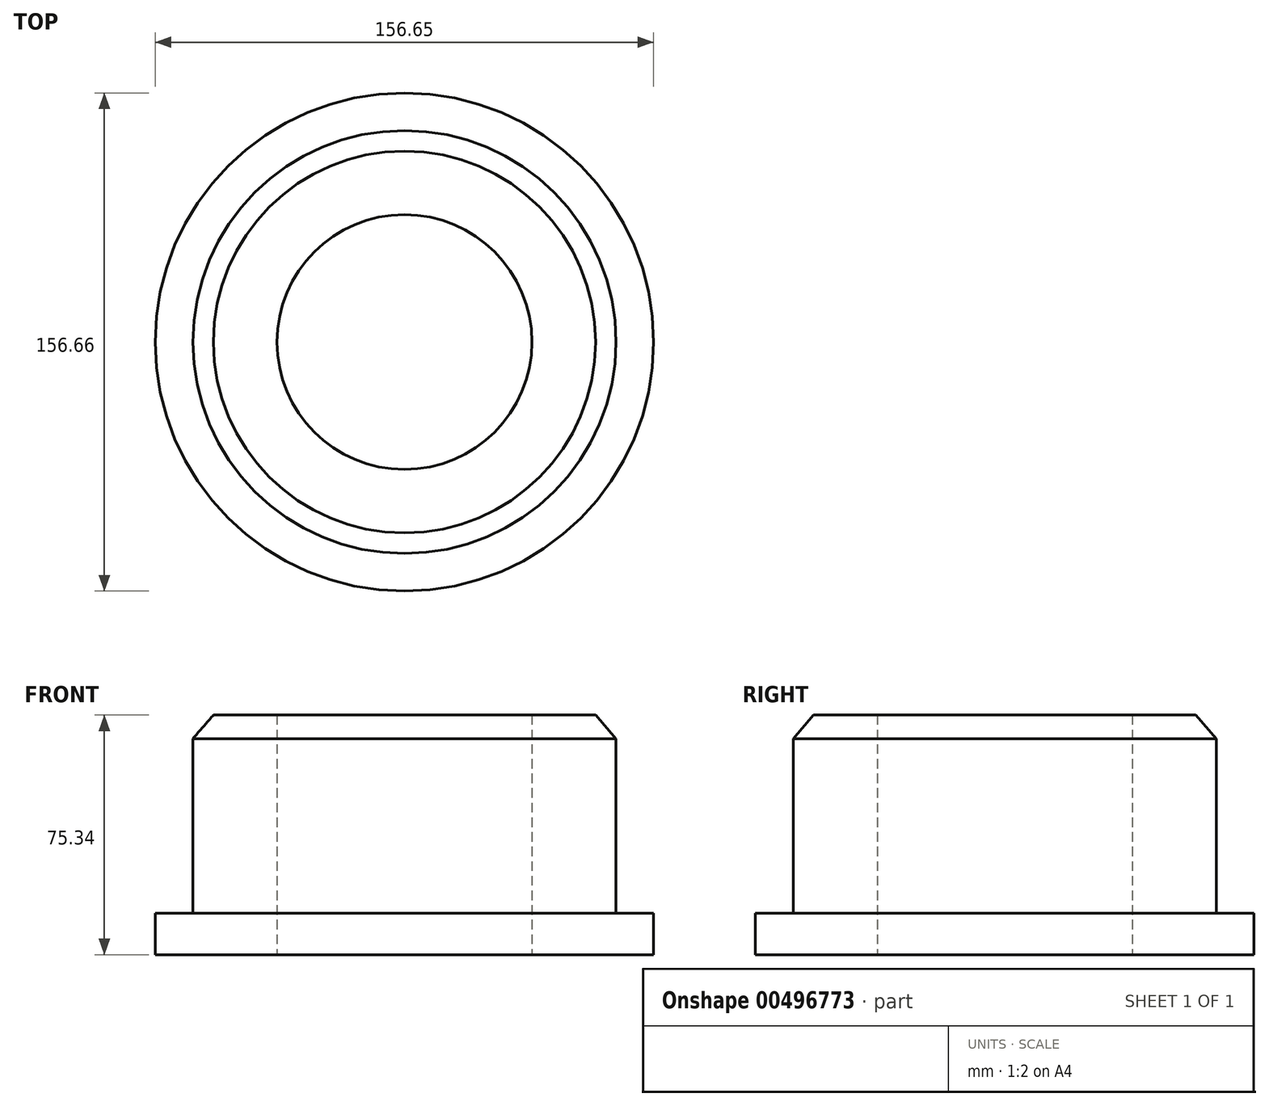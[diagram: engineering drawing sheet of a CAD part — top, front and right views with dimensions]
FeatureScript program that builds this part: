
annotation { "Feature Type Name" : "Feature", "Feature Type Description" : "" }
export const myFeature = defineFeature(function(context is Context, id is Id, definition is map)
    precondition{}
    {
        {
            var Q0;
            Q0=qCreatedBy(makeId("Front.planeOp"),FACE);
            var sketch = newSketch(context, id + "F0", { "sketchPlane" : qUnion([Q0])});
            skLineSegment(sketch, "E0", {"start": v(0, 75.34) * mm, "end": v(19.98, 75.34) * mm});
            skLineSegment(sketch, "E1", {"start": v(19.98, 75.34) * mm, "end": v(19.98, 75.34) * mm});
            skLineSegment(sketch, "E2", {"start": v(26.43, 67.94) * mm, "end": v(19.98, 75.34) * mm});
            skLineSegment(sketch, "E3", {"start": v(26.43, 67.94) * mm, "end": v(26.43, 12.8) * mm});
            skLineSegment(sketch, "E4.bottom", {"start": v(26.28, 13.02) * mm, "end": v(38.25, 13.02) * mm});
            skLineSegment(sketch, "E4.top", {"start": v(26.28, 0) * mm, "end": v(38.25, 0) * mm});
            skLineSegment(sketch, "E4.right", {"start": v(38.25, 13.02) * mm, "end": v(38.25, 0) * mm});
            skLineSegment(sketch, "E5", {"start": v(0, 0) * mm, "end": v(26.28, 0) * mm});
            skLineSegment(sketch, "E6", {"start": v(0, 0) * mm, "end": v(0, 75.34) * mm});
            skLineSegment(sketch, "E7", {"start": v(-40.08, 0) * mm, "end": v(-40.08, 77.14) * mm, "construction": true});
            skSolve(sketch);
        }
        {
            var Q0;
            Q0 = qSketchRegion(id + "F0", true);
            var Q1;
            Q1=sQuery(id+"F0.wireOp",EDGE,"E7");
            revolve(context, id + "F1", {"entities" : qUnion([Q0]), "axis" : qUnion([Q1]), "revolveType" : RevolveType.FULL});
        }
    });
